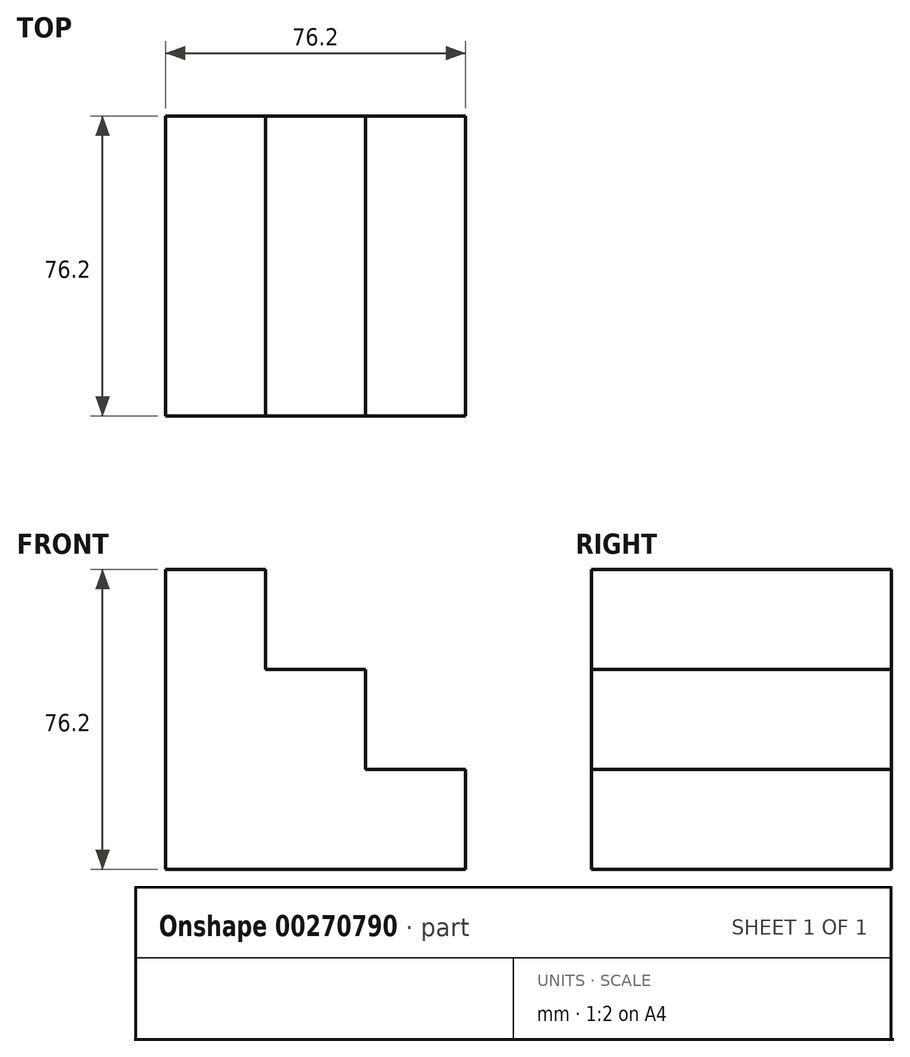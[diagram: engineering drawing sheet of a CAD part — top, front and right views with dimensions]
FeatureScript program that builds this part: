
annotation { "Feature Type Name" : "Feature", "Feature Type Description" : "" }
export const myFeature = defineFeature(function(context is Context, id is Id, definition is map)
    precondition{}
    {
        {
            var Q0;
            Q0=qCreatedBy(makeId("Front.planeOp"),FACE);
            var sketch = newSketch(context, id + "F0", { "sketchPlane" : qUnion([Q0])});
            skLineSegment(sketch, "E0", {"start": v(-53.85, 59.59) * mm, "end": v(-53.85, -16.61) * mm});
            skLineSegment(sketch, "E1", {"start": v(-53.85, -16.61) * mm, "end": v(22.35, -16.61) * mm});
            skLineSegment(sketch, "E2", {"start": v(22.35, -16.61) * mm, "end": v(22.35, 8.79) * mm});
            skLineSegment(sketch, "E3", {"start": v(22.35, 8.79) * mm, "end": v(-3.05, 8.79) * mm});
            skLineSegment(sketch, "E4", {"start": v(-3.05, 8.79) * mm, "end": v(-3.05, 34.19) * mm});
            skLineSegment(sketch, "E5", {"start": v(-3.05, 34.19) * mm, "end": v(-28.45, 34.19) * mm});
            skLineSegment(sketch, "E6", {"start": v(-28.45, 34.19) * mm, "end": v(-28.45, 59.59) * mm});
            skLineSegment(sketch, "E7", {"start": v(-28.45, 59.59) * mm, "end": v(-53.85, 59.59) * mm});
            skSolve(sketch);
        }
        {
            var Q0;
            Q0 = qSketchRegion(id + "F0", true);
            extrude(context, id + "F1", {"entities" : qUnion([Q0]), "depth" : 76.2 * mm});
        }
    });
